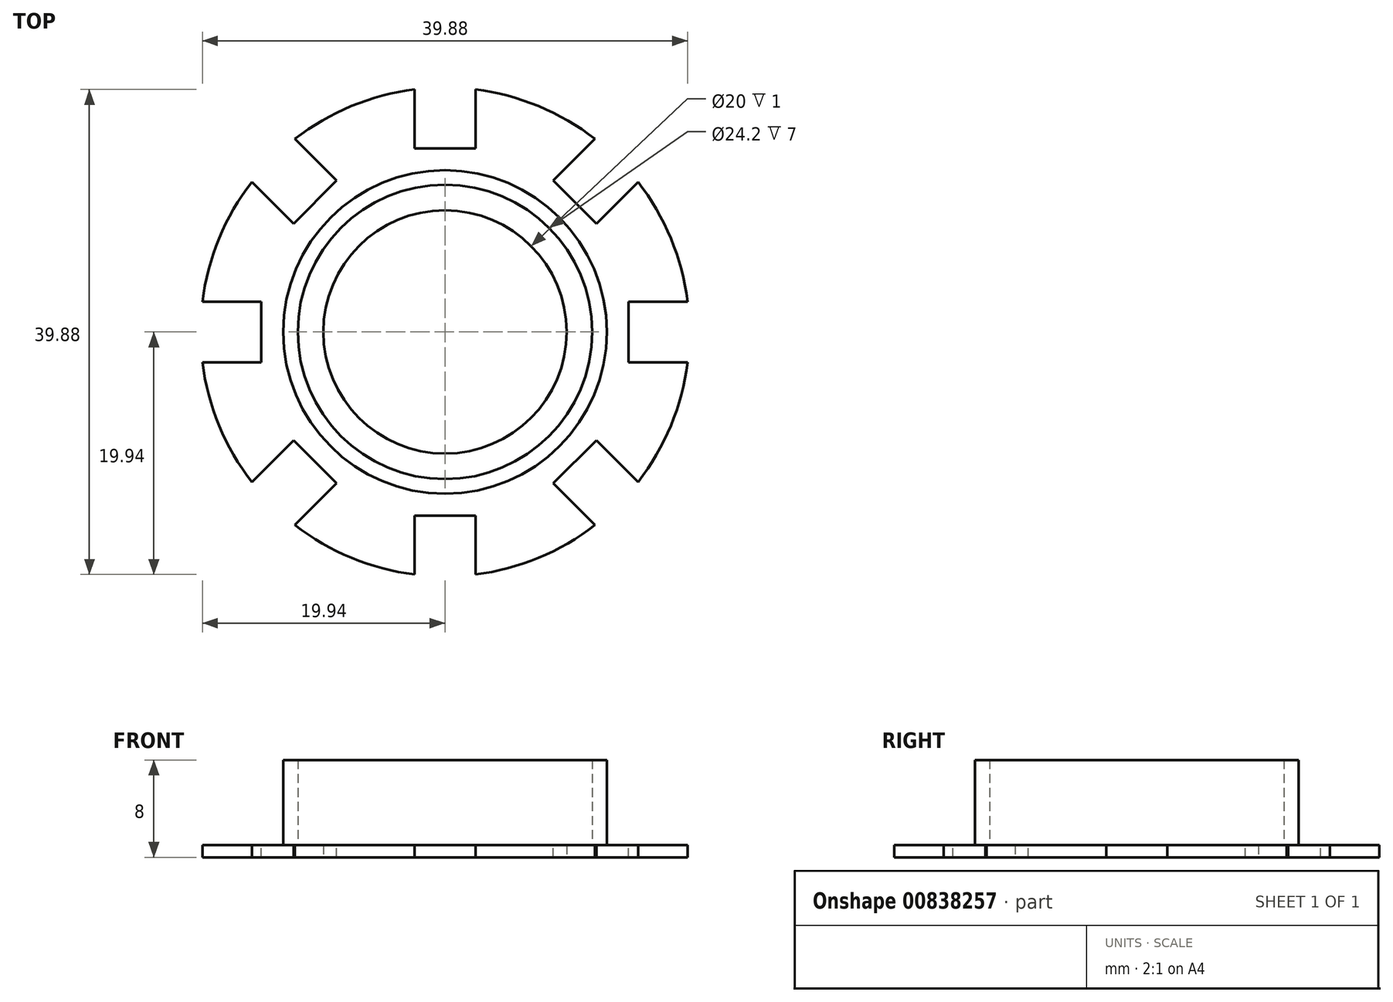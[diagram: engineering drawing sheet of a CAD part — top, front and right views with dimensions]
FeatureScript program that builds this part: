
annotation { "Feature Type Name" : "Feature", "Feature Type Description" : "" }
export const myFeature = defineFeature(function(context is Context, id is Id, definition is map)
    precondition{}
    {
        {
            var Q0;
            Q0=qCreatedBy(makeId("Top.planeOp"),FACE);
            var sketch = newSketch(context, id + "F0", { "sketchPlane" : qUnion([Q0])});
            skCircle(sketch, "E0", {"center": v(0, 0) * mm, "radius": 12.1 * mm});
            skCircle(sketch, "E1.0", {"center": v(0, 0) * mm, "radius": 20.1 * mm});
            skCircle(sketch, "E2", {"center": v(0, 0) * mm, "radius": 10 * mm});
            skCircle(sketch, "E3.0", {"center": v(0, 0) * mm, "radius": 13.3 * mm});
            skSolve(sketch);
        }
        {
            var Q0;
            Q0=makeQuery(id+"F0.imprint","IMPRINT",FACE,{"disambiguationData":[TD([[makeQuery(id+"F0.imprint","IMPRINT",EDGE,{"derivedFrom":sQuery(id+"F0.wireOp",EDGE,"E0")}),-1.0]])]});
            var Q1;
            Q1=makeQuery(id+"F0.imprint","IMPRINT",FACE,{"disambiguationData":[TD([[makeQuery(id+"F0.imprint","IMPRINT",EDGE,{"derivedFrom":sQuery(id+"F0.wireOp",EDGE,"E0")}),1.0]])]});
            var Q2;
            Q2=makeQuery(id+"F0.imprint","IMPRINT",FACE,{"disambiguationData":[TD([[makeQuery(id+"F0.imprint","IMPRINT",EDGE,{"derivedFrom":sQuery(id+"F0.wireOp",EDGE,"E1.0")}),1.0]])]});
            extrude(context, id + "F1", {"entities" : qUnion([Q0, Q1, Q2]), "depth" : 1 * mm, "offsetDistance" : 25 * mm});
        }
        {
            var Q0;
            Q0=makeQuery(id+"F0.imprint","IMPRINT",FACE,{"disambiguationData":[TD([[makeQuery(id+"F0.imprint","IMPRINT",EDGE,{"derivedFrom":sQuery(id+"F0.wireOp",EDGE,"E0")}),-1.0]])]});
            extrude(context, id + "F2", {"entities" : qUnion([Q0]), "operationType" : NewBodyOperationType.ADD, "depth" : 8 * mm, "offsetDistance" : 25 * mm});
        }
        {
            var Q0;
            {var subQ0=sQuery(id+"F0.wireOp",EDGE,"E1.0");Q0=makeQuery(id+"F2.boolean.opBoolean","SPLIT",FACE,{"disambiguationData":[TD([makeQuery(id+"F1.opExtrude","SWEPT_FACE",FACE,{"disambiguationData":[OSD([subQ0])]})])],"derivedFrom":makeQuery(id+"F1.opExtrude","CAP_FACE",FACE,{"disambiguationData":[OSD([subQ0,sQuery(id+"F0.wireOp",EDGE,"E2")])],"isStart":false})});}
            var sketch = newSketch(context, id + "F3", { "sketchPlane" : qUnion([Q0])});
            skLineSegment(sketch, "E4.bottom", {"start": v(2.5, 15.1) * mm, "end": v(-2.5, 15.1) * mm});
            skLineSegment(sketch, "E4.top", {"start": v(2.5, 25.1) * mm, "end": v(-2.5, 25.1) * mm});
            skLineSegment(sketch, "E4.left", {"start": v(2.5, 15.1) * mm, "end": v(2.5, 25.1) * mm});
            skLineSegment(sketch, "E4.right", {"start": v(-2.5, 15.1) * mm, "end": v(-2.5, 25.1) * mm});
            skPoint(sketch, "E4.middle", {"position": v(0, 20.1) * mm});
            skLineSegment(sketch, "E5.1.0", {"start": v(-15.98, 19.52) * mm, "end": v(-19.52, 15.98) * mm});
            skPoint(sketch, "E5.1.1", {"position": v(-14.21, 14.21) * mm});
            skLineSegment(sketch, "E5.1.2", {"start": v(-8.9, 12.45) * mm, "end": v(-12.45, 8.9) * mm});
            skLineSegment(sketch, "E5.1.3", {"start": v(-8.9, 12.45) * mm, "end": v(-15.98, 19.52) * mm});
            skLineSegment(sketch, "E5.1.4", {"start": v(-12.45, 8.9) * mm, "end": v(-19.52, 15.98) * mm});
            skLineSegment(sketch, "E5.2.0", {"start": v(-25.1, 2.5) * mm, "end": v(-25.1, -2.5) * mm});
            skPoint(sketch, "E5.2.1", {"position": v(-20.1, 0) * mm});
            skLineSegment(sketch, "E5.2.2", {"start": v(-15.1, 2.5) * mm, "end": v(-15.1, -2.5) * mm});
            skLineSegment(sketch, "E5.2.3", {"start": v(-15.1, 2.5) * mm, "end": v(-25.1, 2.5) * mm});
            skLineSegment(sketch, "E5.2.4", {"start": v(-15.1, -2.5) * mm, "end": v(-25.1, -2.5) * mm});
            skLineSegment(sketch, "E5.3.0", {"start": v(-19.52, -15.98) * mm, "end": v(-15.98, -19.52) * mm});
            skPoint(sketch, "E5.3.1", {"position": v(-14.21, -14.21) * mm});
            skLineSegment(sketch, "E5.3.2", {"start": v(-12.45, -8.9) * mm, "end": v(-8.9, -12.45) * mm});
            skLineSegment(sketch, "E5.3.3", {"start": v(-12.45, -8.9) * mm, "end": v(-19.52, -15.98) * mm});
            skLineSegment(sketch, "E5.3.4", {"start": v(-8.9, -12.45) * mm, "end": v(-15.98, -19.52) * mm});
            skLineSegment(sketch, "E5.4.0", {"start": v(-2.5, -25.1) * mm, "end": v(2.5, -25.1) * mm});
            skPoint(sketch, "E5.4.1", {"position": v(0, -20.1) * mm});
            skLineSegment(sketch, "E5.4.2", {"start": v(-2.5, -15.1) * mm, "end": v(2.5, -15.1) * mm});
            skLineSegment(sketch, "E5.4.3", {"start": v(-2.5, -15.1) * mm, "end": v(-2.5, -25.1) * mm});
            skLineSegment(sketch, "E5.4.4", {"start": v(2.5, -15.1) * mm, "end": v(2.5, -25.1) * mm});
            skLineSegment(sketch, "E5.5.0", {"start": v(15.98, -19.52) * mm, "end": v(19.52, -15.98) * mm});
            skPoint(sketch, "E5.5.1", {"position": v(14.21, -14.21) * mm});
            skLineSegment(sketch, "E5.5.2", {"start": v(8.9, -12.45) * mm, "end": v(12.45, -8.9) * mm});
            skLineSegment(sketch, "E5.5.3", {"start": v(8.9, -12.45) * mm, "end": v(15.98, -19.52) * mm});
            skLineSegment(sketch, "E5.5.4", {"start": v(12.45, -8.9) * mm, "end": v(19.52, -15.98) * mm});
            skLineSegment(sketch, "E5.6.0", {"start": v(25.1, -2.5) * mm, "end": v(25.1, 2.5) * mm});
            skPoint(sketch, "E5.6.1", {"position": v(20.1, 0) * mm});
            skLineSegment(sketch, "E5.6.2", {"start": v(15.1, -2.5) * mm, "end": v(15.1, 2.5) * mm});
            skLineSegment(sketch, "E5.6.3", {"start": v(15.1, -2.5) * mm, "end": v(25.1, -2.5) * mm});
            skLineSegment(sketch, "E5.6.4", {"start": v(15.1, 2.5) * mm, "end": v(25.1, 2.5) * mm});
            skLineSegment(sketch, "E5.7.0", {"start": v(19.52, 15.98) * mm, "end": v(15.98, 19.52) * mm});
            skPoint(sketch, "E5.7.1", {"position": v(14.21, 14.21) * mm});
            skLineSegment(sketch, "E5.7.2", {"start": v(12.45, 8.9) * mm, "end": v(8.9, 12.45) * mm});
            skLineSegment(sketch, "E5.7.3", {"start": v(12.45, 8.9) * mm, "end": v(19.52, 15.98) * mm});
            skLineSegment(sketch, "E5.7.4", {"start": v(8.9, 12.45) * mm, "end": v(15.98, 19.52) * mm});
            skPoint(sketch, "E5.center", {"position": v(0, 0) * mm});
            skSolve(sketch);
        }
        {
            var Q0;
            Q0=qSketchRegion(id+"F3",true);
            extrude(context, id + "F4", {"entities" : qUnion([Q0]), "operationType" : NewBodyOperationType.REMOVE, "endBound" : BoundingType.THROUGH_ALL, "oppositeDirection" : true, "depth" : 25 * mm, "offsetDistance" : 25 * mm});
        }
    });
